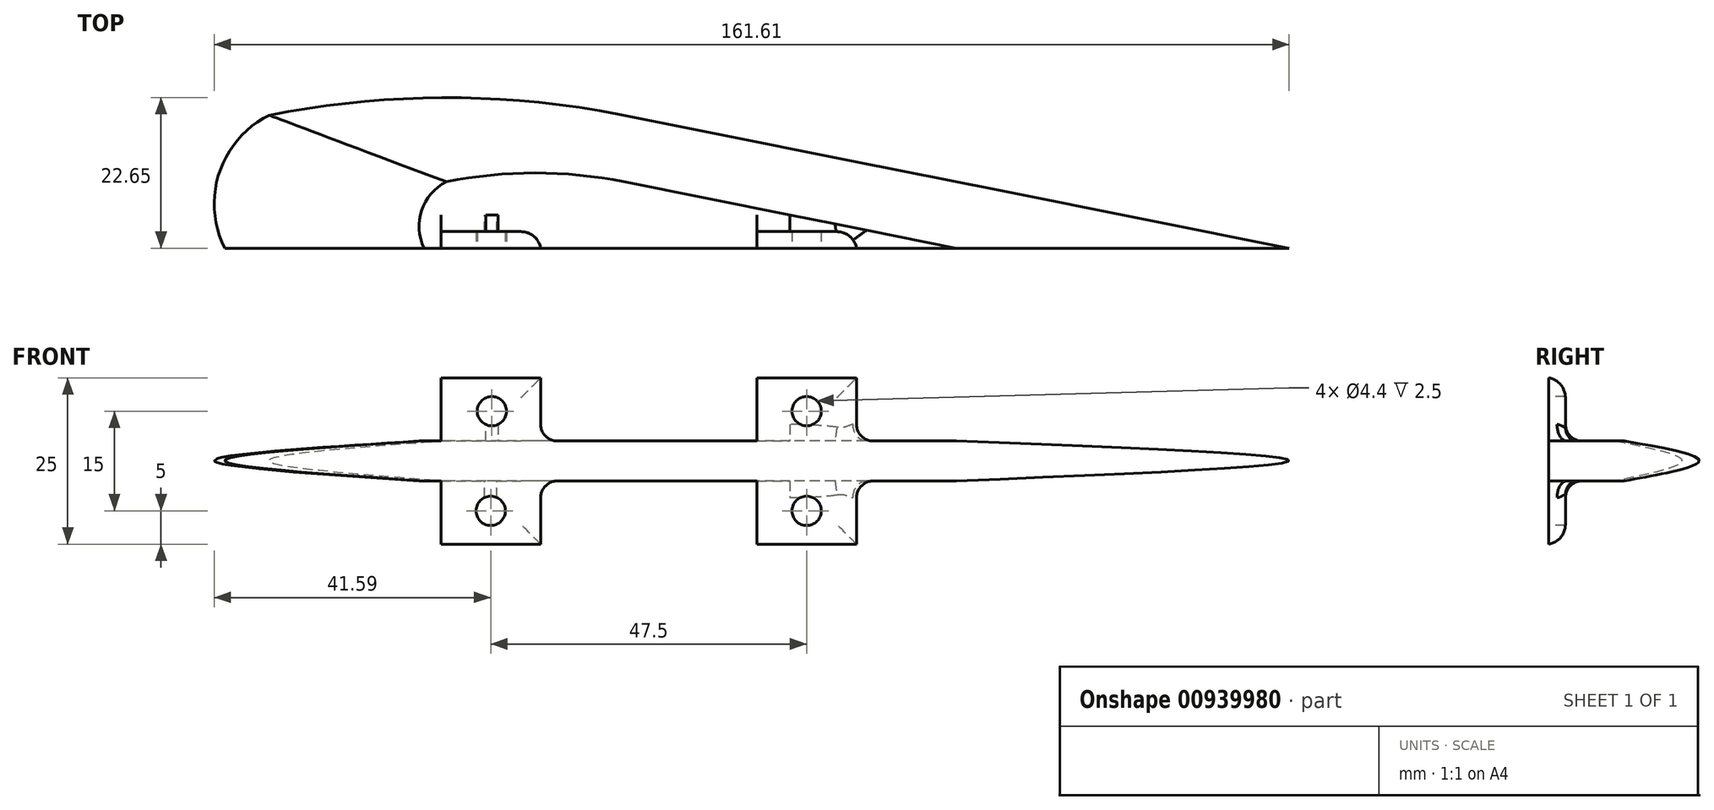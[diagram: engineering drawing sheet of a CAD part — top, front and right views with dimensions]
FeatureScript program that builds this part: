
annotation { "Feature Type Name" : "Feature", "Feature Type Description" : "" }
export const myFeature = defineFeature(function(context is Context, id is Id, definition is map)
    precondition{}
    {
        {
            var Q0;
            Q0=qCreatedBy(makeId("Top.planeOp"),FACE);
            var sketch = newSketch(context, id + "F0", { "sketchPlane" : qUnion([Q0])});
            skLineSegment(sketch, "E0", {"start": v(-60, 0) * mm, "end": v(100, 0) * mm});
            skArc(sketch, "E1", {"start": v(-53.33, 20) * mm, "mid": v(-60.8, 11.38) * mm, "end": v(-60, 0) * mm});
            skLineSegment(sketch, "E2", {"start": v(100, 0) * mm, "end": v(0, 20) * mm});
            skArc(sketch, "E3", {"start": v(0, 20) * mm, "mid": v(-26.67, 22.64) * mm, "end": v(-53.33, 20) * mm});
            skSolve(sketch);
        }
        {
            var Q0;
            Q0=qCreatedBy(makeId("Top.planeOp"),FACE);
            cPlane(context, id + "F1", {"entities" : qUnion([Q0]), "cplaneType" : CPlaneType.OFFSET, "offset" : 3 * mm, "width" : 150 * mm, "height" : 150 * mm});
        }
        {
            var Q0;
            Q0=qCreatedBy(id+"F1.planeOp",FACE);
            var sketch = newSketch(context, id + "F2", { "sketchPlane" : qUnion([Q0])});
            skLineSegment(sketch, "E4", {"start": v(50, 0) * mm, "end": v(-30, 0) * mm});
            skArc(sketch, "E5", {"start": v(-26.67, 10) * mm, "mid": v(-30.4, 5.7) * mm, "end": v(-30, 0) * mm});
            skLineSegment(sketch, "E6", {"start": v(50, 0) * mm, "end": v(0, 10) * mm});
            skArc(sketch, "E7", {"start": v(0, 10) * mm, "mid": v(-13.33, 11.32) * mm, "end": v(-26.67, 10) * mm});
            skSolve(sketch);
        }
        {
            var Q0;
            Q0=qCreatedBy(makeId("Top.planeOp"),FACE);
            cPlane(context, id + "F3", {"entities" : qUnion([Q0]), "cplaneType" : CPlaneType.OFFSET, "offset" : 3 * mm, "oppositeDirection" : true, "width" : 150 * mm, "height" : 150 * mm});
        }
        {
            var Q0;
            Q0=qCreatedBy(id+"F3.planeOp",FACE);
            var sketch = newSketch(context, id + "F4", { "sketchPlane" : qUnion([Q0])});
            skLineSegment(sketch, "E8.0.0", {"start": v(50, 0) * mm, "end": v(0, 10) * mm});
            skArc(sketch, "E8.0.1", {"start": v(0, 10) * mm, "mid": v(-13.33, 11.32) * mm, "end": v(-26.67, 10) * mm});
            skArc(sketch, "E8.0.2", {"start": v(-26.67, 10) * mm, "mid": v(-30.4, 5.7) * mm, "end": v(-30, 0) * mm});
            skLineSegment(sketch, "E8.0.3", {"start": v(-30, 0) * mm, "end": v(50, 0) * mm});
            skSolve(sketch);
        }
        {
            var Q0;
            Q0 = qSketchRegion(id + "F2", true);
            var Q1;
            Q1 = qSketchRegion(id + "F0", true);
            var Q2;
            Q2 = qSketchRegion(id + "F4", true);
            loft(context, id + "F5", {"sheetProfilesArray" : [{ "sheetProfileEntities" : qUnion([Q0]) }, { "sheetProfileEntities" : qUnion([Q1]) }, { "sheetProfileEntities" : qUnion([Q2]) }]});
        }
        {
            var Q0;
            Q0=qCreatedBy(makeId("Front.planeOp"),FACE);
            var sketch = newSketch(context, id + "F6", { "sketchPlane" : qUnion([Q0])});
            skLineSegment(sketch, "E9.bottom", {"start": v(-12.5, 0) * mm, "end": v(-27.5, 0) * mm});
            skLineSegment(sketch, "E9.top", {"start": v(-12.5, 12.5) * mm, "end": v(-27.5, 12.5) * mm});
            skLineSegment(sketch, "E9.left", {"start": v(-12.5, 0) * mm, "end": v(-12.5, 12.5) * mm});
            skLineSegment(sketch, "E9.right", {"start": v(-27.5, 0) * mm, "end": v(-27.5, 12.5) * mm});
            skPoint(sketch, "E9.middle", {"position": v(-20, 6.25) * mm});
            skCircle(sketch, "E10", {"center": v(-19.84, 7.5) * mm, "radius": 2.2 * mm});
            skLineSegment(sketch, "E11.MirrorCS", {"start": v(-12.5, 0) * mm, "end": v(-12.5, -12.5) * mm});
            skLineSegment(sketch, "E12.MirrorCS", {"start": v(-12.5, -12.5) * mm, "end": v(-27.5, -12.5) * mm});
            skLineSegment(sketch, "E13.MirrorCS", {"start": v(-27.5, 0) * mm, "end": v(-27.5, -12.5) * mm});
            skCircle(sketch, "E14.MirrorC", {"center": v(-20, -7.5) * mm, "radius": 2.2 * mm});
            skLineSegment(sketch, "E15.bottom", {"start": v(35, 0) * mm, "end": v(20, 0) * mm});
            skLineSegment(sketch, "E15.top", {"start": v(35, 12.5) * mm, "end": v(20, 12.5) * mm});
            skLineSegment(sketch, "E15.left", {"start": v(35, 0) * mm, "end": v(35, 12.5) * mm});
            skLineSegment(sketch, "E15.right", {"start": v(20, 0) * mm, "end": v(20, 12.5) * mm});
            skPoint(sketch, "E15.middle", {"position": v(27.5, 6.25) * mm});
            skCircle(sketch, "E16", {"center": v(27.5, 7.5) * mm, "radius": 2.2 * mm});
            skLineSegment(sketch, "E17.MirrorCS", {"start": v(35, 0) * mm, "end": v(35, -12.5) * mm});
            skLineSegment(sketch, "E18.MirrorCS", {"start": v(35, -12.5) * mm, "end": v(20, -12.5) * mm});
            skLineSegment(sketch, "E19.MirrorCS", {"start": v(20, 0) * mm, "end": v(20, -12.5) * mm});
            skCircle(sketch, "E20.MirrorC", {"center": v(27.5, -7.5) * mm, "radius": 2.2 * mm});
            skSolve(sketch);
        }
        {
            var Q0;
            Q0 = qSketchRegion(id + "F6", true);
            extrude(context, id + "F7", {"entities" : qUnion([Q0]), "operationType" : NewBodyOperationType.ADD, "oppositeDirection" : true, "depth" : 2.5 * mm, "offsetDistance" : 25 * mm});
        }
        {
            var Q0;
            Q0=makeQuery(id+"F7.opExtrude","CAP_EDGE",EDGE,{"disambiguationData":[OSD([sQuery(id+"F6.wireOp",EDGE,"E9.top")])],"isStart":false});
            var Q1;
            Q1=makeQuery(id+"F7.opExtrude","CAP_EDGE",EDGE,{"disambiguationData":[OSD([sQuery(id+"F6.wireOp",EDGE,"E12.MirrorCS")])],"isStart":false});
            var Q2;
            Q2=makeQuery(id+"F7.opExtrude","CAP_EDGE",EDGE,{"disambiguationData":[OSD([sQuery(id+"F6.wireOp",EDGE,"E15.top")])],"isStart":false});
            var Q3;
            Q3=makeQuery(id+"F7.opExtrude","CAP_EDGE",EDGE,{"disambiguationData":[OSD([sQuery(id+"F6.wireOp",EDGE,"E18.MirrorCS")])],"isStart":false});
            var Q4;
            {var subQ0=sQuery(id+"F6.wireOp",EDGE,"E15.top");var subQ1=sQuery(id+"F6.wireOp",EDGE,"E17.MirrorCS");var subQ2=sQuery(id+"F6.wireOp",EDGE,"E15.left");Q4=makeQuery(id+"F7.boolean.opBoolean","SPLIT",EDGE,{"disambiguationData":[TD([makeQuery(id+"F7.opExtrude","SWEPT_FACE",FACE,{"disambiguationData":[OSD([subQ0])]})])],"derivedFrom":makeQuery(id+"F7.opExtrude","CAP_EDGE",EDGE,{"disambiguationData":[OSD([subQ2,subQ1])],"isStart":false})});}
            var Q5;
            {var subQ0=sQuery(id+"F6.wireOp",EDGE,"E18.MirrorCS");var subQ1=sQuery(id+"F6.wireOp",EDGE,"E17.MirrorCS");var subQ2=sQuery(id+"F6.wireOp",EDGE,"E15.left");Q5=makeQuery(id+"F7.boolean.opBoolean","SPLIT",EDGE,{"disambiguationData":[TD([makeQuery(id+"F7.opExtrude","SWEPT_FACE",FACE,{"disambiguationData":[OSD([subQ0])]})])],"derivedFrom":makeQuery(id+"F7.opExtrude","CAP_EDGE",EDGE,{"disambiguationData":[OSD([subQ2,subQ1])],"isStart":false})});}
            var Q6;
            {var subQ0=sQuery(id+"F6.wireOp",EDGE,"E12.MirrorCS");var subQ1=sQuery(id+"F6.wireOp",EDGE,"E11.MirrorCS");var subQ2=sQuery(id+"F6.wireOp",EDGE,"E9.left");Q6=makeQuery(id+"F7.boolean.opBoolean","SPLIT",EDGE,{"disambiguationData":[TD([makeQuery(id+"F7.opExtrude","SWEPT_FACE",FACE,{"disambiguationData":[OSD([subQ0])]})])],"derivedFrom":makeQuery(id+"F7.opExtrude","CAP_EDGE",EDGE,{"disambiguationData":[OSD([subQ2,subQ1])],"isStart":false})});}
            var Q7;
            {var subQ0=sQuery(id+"F6.wireOp",EDGE,"E9.top");var subQ1=sQuery(id+"F6.wireOp",EDGE,"E11.MirrorCS");var subQ2=sQuery(id+"F6.wireOp",EDGE,"E9.left");Q7=makeQuery(id+"F7.boolean.opBoolean","SPLIT",EDGE,{"disambiguationData":[TD([makeQuery(id+"F7.opExtrude","SWEPT_FACE",FACE,{"disambiguationData":[OSD([subQ0])]})])],"derivedFrom":makeQuery(id+"F7.opExtrude","CAP_EDGE",EDGE,{"disambiguationData":[OSD([subQ2,subQ1])],"isStart":false})});}
            fillet(context, id + "F8", {"entities" : qUnion([Q0, Q1, Q2, Q3, Q4, Q5, Q6, Q7]), "radius" : 3 * mm, "tangentPropagation" : true, "allowEdgeOverflow" : false});
        }
        {
            var Q0;
            Q0=makeQuery(id+"F7.boolean.opBoolean","INTERSECT",EDGE,{"derivedFrom":[makeQuery(id+"F5.opLoft","CAP_FACE",FACE,{"disambiguationData":[OSD([makeQuery(id+"F4.imprint","IMPRINT",FACE,{"disambiguationData":[TD([[makeQuery(id+"F4.imprint","IMPRINT",EDGE,{"derivedFrom":sQuery(id+"F4.wireOp",EDGE,"E8.0.0")}),1.0]])]})])],"isStart":true}),makeQuery(id+"F7.opExtrude","CAP_FACE",FACE,{"disambiguationData":[OSD([sQuery(id+"F6.wireOp",EDGE,"E9.top"),sQuery(id+"F6.wireOp",EDGE,"E9.left"),sQuery(id+"F6.wireOp",EDGE,"E9.right"),sQuery(id+"F6.wireOp",EDGE,"E10"),sQuery(id+"F6.wireOp",EDGE,"E11.MirrorCS"),sQuery(id+"F6.wireOp",EDGE,"E12.MirrorCS"),sQuery(id+"F6.wireOp",EDGE,"E13.MirrorCS"),sQuery(id+"F6.wireOp",EDGE,"E14.MirrorC")])],"isStart":false})]});
            var Q1;
            Q1=makeQuery(id+"F7.boolean.opBoolean","INTERSECT",EDGE,{"derivedFrom":[makeQuery(id+"F5.opLoft","CAP_FACE",FACE,{"disambiguationData":[OSD([makeQuery(id+"F4.imprint","IMPRINT",FACE,{"disambiguationData":[TD([[makeQuery(id+"F4.imprint","IMPRINT",EDGE,{"derivedFrom":sQuery(id+"F4.wireOp",EDGE,"E8.0.0")}),1.0]])]})])],"isStart":true}),makeQuery(id+"F7.opExtrude","CAP_FACE",FACE,{"disambiguationData":[OSD([sQuery(id+"F6.wireOp",EDGE,"E15.top"),sQuery(id+"F6.wireOp",EDGE,"E15.left"),sQuery(id+"F6.wireOp",EDGE,"E15.right"),sQuery(id+"F6.wireOp",EDGE,"E16"),sQuery(id+"F6.wireOp",EDGE,"E17.MirrorCS"),sQuery(id+"F6.wireOp",EDGE,"E18.MirrorCS"),sQuery(id+"F6.wireOp",EDGE,"E19.MirrorCS"),sQuery(id+"F6.wireOp",EDGE,"E20.MirrorC")])],"isStart":false})]});
            var Q2;
            Q2=makeQuery(id+"F7.boolean.opBoolean","INTERSECT",EDGE,{"derivedFrom":[makeQuery(id+"F5.opLoft","CAP_FACE",FACE,{"disambiguationData":[OSD([makeQuery(id+"F2.imprint","IMPRINT",FACE,{"disambiguationData":[TD([[makeQuery(id+"F2.imprint","IMPRINT",EDGE,{"derivedFrom":sQuery(id+"F2.wireOp",EDGE,"E4")}),-1.0]])]})])],"isStart":true}),makeQuery(id+"F7.opExtrude","CAP_FACE",FACE,{"disambiguationData":[OSD([sQuery(id+"F6.wireOp",EDGE,"E15.top"),sQuery(id+"F6.wireOp",EDGE,"E15.left"),sQuery(id+"F6.wireOp",EDGE,"E15.right"),sQuery(id+"F6.wireOp",EDGE,"E16"),sQuery(id+"F6.wireOp",EDGE,"E17.MirrorCS"),sQuery(id+"F6.wireOp",EDGE,"E18.MirrorCS"),sQuery(id+"F6.wireOp",EDGE,"E19.MirrorCS"),sQuery(id+"F6.wireOp",EDGE,"E20.MirrorC")])],"isStart":false})]});
            var Q3;
            Q3=makeQuery(id+"F7.boolean.opBoolean","INTERSECT",EDGE,{"derivedFrom":[makeQuery(id+"F5.opLoft","CAP_FACE",FACE,{"disambiguationData":[OSD([makeQuery(id+"F2.imprint","IMPRINT",FACE,{"disambiguationData":[TD([[makeQuery(id+"F2.imprint","IMPRINT",EDGE,{"derivedFrom":sQuery(id+"F2.wireOp",EDGE,"E4")}),-1.0]])]})])],"isStart":true}),makeQuery(id+"F7.opExtrude","CAP_FACE",FACE,{"disambiguationData":[OSD([sQuery(id+"F6.wireOp",EDGE,"E9.top"),sQuery(id+"F6.wireOp",EDGE,"E9.left"),sQuery(id+"F6.wireOp",EDGE,"E9.right"),sQuery(id+"F6.wireOp",EDGE,"E10"),sQuery(id+"F6.wireOp",EDGE,"E11.MirrorCS"),sQuery(id+"F6.wireOp",EDGE,"E12.MirrorCS"),sQuery(id+"F6.wireOp",EDGE,"E13.MirrorCS"),sQuery(id+"F6.wireOp",EDGE,"E14.MirrorC")])],"isStart":false})]});
            fillet(context, id + "F9", {"entities" : qUnion([Q0, Q1, Q2, Q3]), "radius" : 2.5 * mm, "tangentPropagation" : true, "allowEdgeOverflow" : false});
        }
    });
